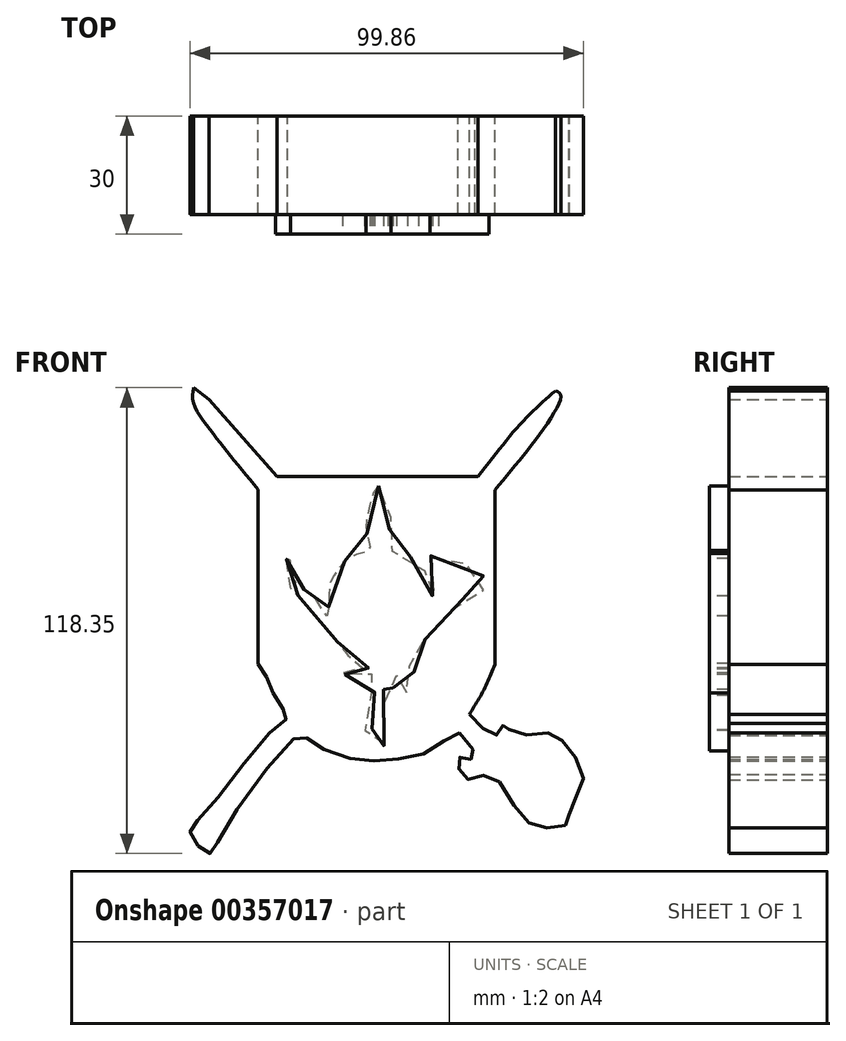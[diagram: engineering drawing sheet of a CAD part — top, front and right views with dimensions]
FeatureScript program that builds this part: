
annotation { "Feature Type Name" : "Feature", "Feature Type Description" : "" }
export const myFeature = defineFeature(function(context is Context, id is Id, definition is map)
    precondition{}
    {
        {
            var Q0;
            Q0=qCreatedBy(makeId("Front.planeOp"),FACE);
            var sketch = newSketch(context, id + "F0", { "sketchPlane" : qUnion([Q0])});
            skFitSpline(sketch, "E0", {"points": [v(24.36, 49.57) * mm, v(25.78, 48.44) * mm, v(20.11, 38.24) * mm, v(9.06, 24.36) * mm], "startDerivative": vector(12.88, -4.69) * mm, "endDerivative": vector(-23.52, -28.34) * mm});
            skLineSegment(sketch, "E1", {"start": v(9.06, 24.36) * mm, "end": v(9.06, -17.28) * mm});
            skFitSpline(sketch, "E2", {"points": [v(9.06, -17.28) * mm, v(9.06, -21.25) * mm], "startDerivative": vector(0, -3.97) * mm, "endDerivative": vector(0, -3.97) * mm});
            skFitSpline(sketch, "E3", {"points": [v(9.06, -19.92) * mm, v(5.95, -26.91) * mm, v(2.55, -32.58) * mm, v(0, -37.4) * mm], "startDerivative": vector(-8.1, -19.98) * mm, "endDerivative": vector(-7.84, -15.7) * mm});
            skFitSpline(sketch, "E4", {"points": [v(24.36, 49.57) * mm, v(16.06, 41.77) * mm, v(4.76, 27.8) * mm], "startDerivative": vector(-18.39, -15.94) * mm, "endDerivative": vector(-20.73, -27.2) * mm});
            skLineSegment(sketch, "E5", {"start": v(4.76, 27.8) * mm, "end": v(-46.39, 27.8) * mm});
            skLineSegment(sketch, "E6", {"start": v(-46.39, 27.8) * mm, "end": v(-63.63, 47.42) * mm});
            skLineSegment(sketch, "E7", {"start": v(-63.63, 47.42) * mm, "end": v(-67.5, 50.4) * mm});
            skFitSpline(sketch, "E8", {"points": [v(-67.5, 50.4) * mm, v(-67.5, 46.23) * mm, v(-63.34, 39.69) * mm, v(-57.98, 32.85) * mm, v(-51.14, 24.52) * mm], "startDerivative": vector(-3.6, -21.72) * mm, "endDerivative": vector(23.96, -28.81) * mm});
            skLineSegment(sketch, "E9", {"start": v(-51.14, 24.52) * mm, "end": v(-51.14, -13.24) * mm});
            skFitSpline(sketch, "E10", {"points": [v(-51.14, -13.24) * mm, v(-51.14, -19.78) * mm], "startDerivative": vector(0, -6.54) * mm, "endDerivative": vector(0, -6.54) * mm});
            skFitSpline(sketch, "E11", {"points": [v(-51.14, -19.78) * mm, v(-48.77, -23.65) * mm, v(-46.39, -29) * mm, v(-43.71, -33.16) * mm, v(-46.98, -36.14) * mm, v(-64.82, -57.84) * mm, v(-68.4, -62) * mm, v(-66.3, -66.17) * mm, v(-63.34, -67.95) * mm, v(-60.66, -63.5) * mm, v(-40.74, -37.92) * mm, v(-38.36, -39.11) * mm, v(-27.65, -43.87) * mm, v(-16.95, -44.17) * mm, v(-5.65, -40.9) * mm, v(0, -37.4) * mm, v(3.87, -43.57) * mm, v(2.08, -43.87) * mm, v(0, -43.57) * mm, v(0, -46.84) * mm, v(2.68, -49.22) * mm, v(8.03, -48.03) * mm, v(15.46, -58.14) * mm, v(22, -61.41) * mm, v(27.65, -60.22) * mm, v(27.95, -56.95) * mm, v(31.44, -49.22) * mm, v(27.06, -40.3) * mm, v(22.6, -37.4) * mm, v(13.68, -37.4) * mm, v(11.3, -34.95) * mm, v(10.4, -37.4) * mm, v(7.73, -37.4) * mm, v(2.55, -32.58) * mm], "startDerivative": vector(101.67, -143.54) * mm, "endDerivative": vector(-163.62, 184.73) * mm});
            skSolve(sketch);
        }
        {
            var Q0;
            Q0=qCreatedBy(makeId("Front.planeOp"),FACE);
            var sketch = newSketch(context, id + "F1", { "sketchPlane" : qUnion([Q0])});
            skFitSpline(sketch, "E12", {"points": [v(-20.52, 25.41) * mm, v(-23.2, 18.87) * mm, v(-23.5, 13.52) * mm, v(-22.9, 9.06) * mm, v(-27.36, 7.57) * mm, v(-31.52, 3.11) * mm, v(-33, 0) * mm, v(-33.6, -7.6) * mm, v(-36.87, -2.83) * mm, v(-40.74, 0) * mm, v(-43.12, 4.9) * mm, v(-43.12, 6.98) * mm, v(-46.68, 4) * mm, v(-43.41, 0) * mm, v(-37.76, -6.4) * mm, v(-31.22, -13.84) * mm, v(-27.36, -18.3) * mm, v(-22.6, -20.68) * mm, v(-27.06, -20.38) * mm, v(-29.44, -19.78) * mm, v(-29.44, -22.16) * mm, v(-26.76, -21.87) * mm, v(-22.6, -21.87) * mm, v(-21.7, -27.81) * mm, v(-22.3, -26.33) * mm, v(-22.3, -36.44) * mm, v(-24.09, -36.73) * mm, v(-21.11, -41.79) * mm, v(-18.44, -38.81) * mm, v(-18.44, -33.76) * mm, v(-18.44, -22.76) * mm, v(-16.06, -22.46) * mm, v(-16.65, -24.84) * mm, v(-16.35, -26.92) * mm, v(-10.7, -25.73) * mm, v(-11.9, -21.27) * mm, v(-13.08, -18.6) * mm, v(-9.81, -14.73) * mm, v(-7.14, -11.46) * mm, v(0, -4.32) * mm, v(2.08, -2.54) * mm, v(7.43, 0) * mm, v(5.05, 3.4) * mm, v(-4.76, 8.17) * mm, v(-7.43, 7.27) * mm, v(-5.35, 2.52) * mm, v(-6.84, -2.54) * mm, v(-6.84, 0) * mm, v(-9.81, 4.9) * mm, v(-15.76, 9.06) * mm, v(-17.84, 8.76) * mm, v(-17.54, 16.2) * mm, v(-17.84, 20.66) * mm, v(-20.52, 25.41) * mm]});
            skSolve(sketch);
        }
        {
            var Q0;
            Q0=qCreatedBy(makeId("Front.planeOp"),FACE);
            var sketch = newSketch(context, id + "F2", { "sketchPlane" : qUnion([Q0])});
            skArc(sketch, "E13", {"start": v(-22.6, 6.09) * mm, "mid": v(-31.52, -5.1) * mm, "end": v(-22.9, -16.51) * mm});
            skLineSegment(sketch, "E14", {"start": v(-22.6, 6.09) * mm, "end": v(-22.9, -16.51) * mm});
            skArc(sketch, "E15", {"start": v(-16.95, -15.62) * mm, "mid": v(-8.75, -4.16) * mm, "end": v(-18.44, 6.09) * mm});
            skLineSegment(sketch, "E16", {"start": v(-18.44, 6.09) * mm, "end": v(-16.95, -15.62) * mm});
            skSolve(sketch);
        }
        {
            var Q0;
            Q0 = qSketchRegion(id + "F0", true);
            extrude(context, id + "F3", {"entities" : qUnion([Q0]), "depth" : 25 * mm});
        }
        {
            var Q0;
            Q0 = qSketchRegion(id + "F1", true);
            var Q1;
            Q1 = qSketchRegion(id + "F2", true);
            extrude(context, id + "F4", {"entities" : qUnion([Q0, Q1]), "operationType" : NewBodyOperationType.ADD, "depth" : 30 * mm});
        }
        {
            var Q0;
            Q0 = qSketchRegion(id + "F2", true);
            extrude(context, id + "F5", {"entities" : qUnion([Q0]), "operationType" : NewBodyOperationType.ADD, "depth" : 27.5 * mm});
        }
    });
